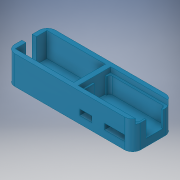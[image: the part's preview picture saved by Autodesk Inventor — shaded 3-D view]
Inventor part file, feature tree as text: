
AUTODESK INVENTOR PART (.ipt)
format: ipt  version: 2019 (Build 230136000, 136)  size: 219,136 bytes
history: native  units: in
note: dims shown in document units (in); Inventor stores cm internally (conversion verified against a paired STEP export)
features: extrude x5, sketch x5, fillet x2
ambient origin geometry x8: Origin, YZ Plane, XZ Plane, XY Plane, X Axis, Y Axis, Z Axis, Center Point
bodies: Body1 (feature_tree)
feature tree (12):
  extrude  "Extrusion2"  Depth=1.9685in
  extrude  "Extrusion3"  Depth=2.8346in
  extrude  "Extrusion5"  Depth=1.0236in TaperAngle=0.0deg
  fillet  "Fillet2"  Radius=2.6772in
  extrude  "Extrusion7"  Depth=0.8in
  extrude  "Extrusion8"  Depth=0.1181in
  fillet  "Fillet3"  Radius=0.5906in
  sketch  "Sketch2"  dims[d4=6.1024in d5=1.9685in]
  sketch  "Sketch4"  dims[d6=1.378in d7=0.0in d8=2.8346in]
  sketch  "Sketch5"  dims[d9=1.5748in d10=1.0236in d11=0.0in d12=2.6772in]
  sketch  "Sketch7"  dims[d13=1.3386in d17=0.8in]
  sketch  "Sketch9"  dims[d18=0.7874in d19=0.0in d20=0.1181in d29=0.5906in d30=0.2756in d32=0.0in d33=0.25in d34=0.0in d35=0.4882in d36=0.4724in d37=0.2756in d38=0.4724in d39=0.2756in d40=1.6299in d41=2.126in d43=0.5906in d44=0.1575in d45=2.8346in d46=1.5354in d47=0.1969in d48=1.1811in d49=0.0in d50=0.5in d51=0.3937in d52=0.315in]
